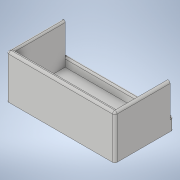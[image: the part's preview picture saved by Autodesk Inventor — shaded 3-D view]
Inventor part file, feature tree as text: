
AUTODESK INVENTOR PART (.ipt)
format: ipt  version: 2022 (Build 260153000, 153)  size: 165,888 bytes
history: native  units: in
note: dims shown in document units (in); Inventor stores cm internally (conversion verified against a paired STEP export)
features: extrude x4, sketch x4, fillet x3
ambient origin geometry x8: Origin, YZ Plane, XZ Plane, XY Plane, X Axis, Y Axis, Z Axis, Center Point
bodies: Solid1 (feature_tree)
feature tree (11):
  extrude  "Extrusion1"  Depth=3.25in
  extrude  "Extrusion2"  TaperAngle=0.0deg  [1 undecoded]
  extrude  "Extrusion3"  Depth=0.5in
  extrude  "Extrusion6"  Depth=0.1875in
  fillet  "Fillet5"  Radius=2.25in
  fillet  "Fillet7"  [1 undecoded]
  fillet  "Fillet8"  Radius=0.1875in
  sketch  "Sketch1"  dims[d0=6.0in d1=3.25in]
  sketch  "Sketch2"  dims[d2=0.1875in d3=0.0in]
  sketch  "Sketch3"  dims[d4=0.1875in d5=0.5in]
  sketch  "Sketch6"  dims[d6=0.0in d7=0.1875in d8=2.25in d9=0.0in d17=0.1875in d18=0.1875in d19=2.25in d20=0.0in d22=0.125in d24=0.125in d25=0.125in]
note: 2 required parameter values undecoded (feature->parameter linkage not recoverable at this tier; creation-order binding heuristic only, values carry confidence <= 0.55)
